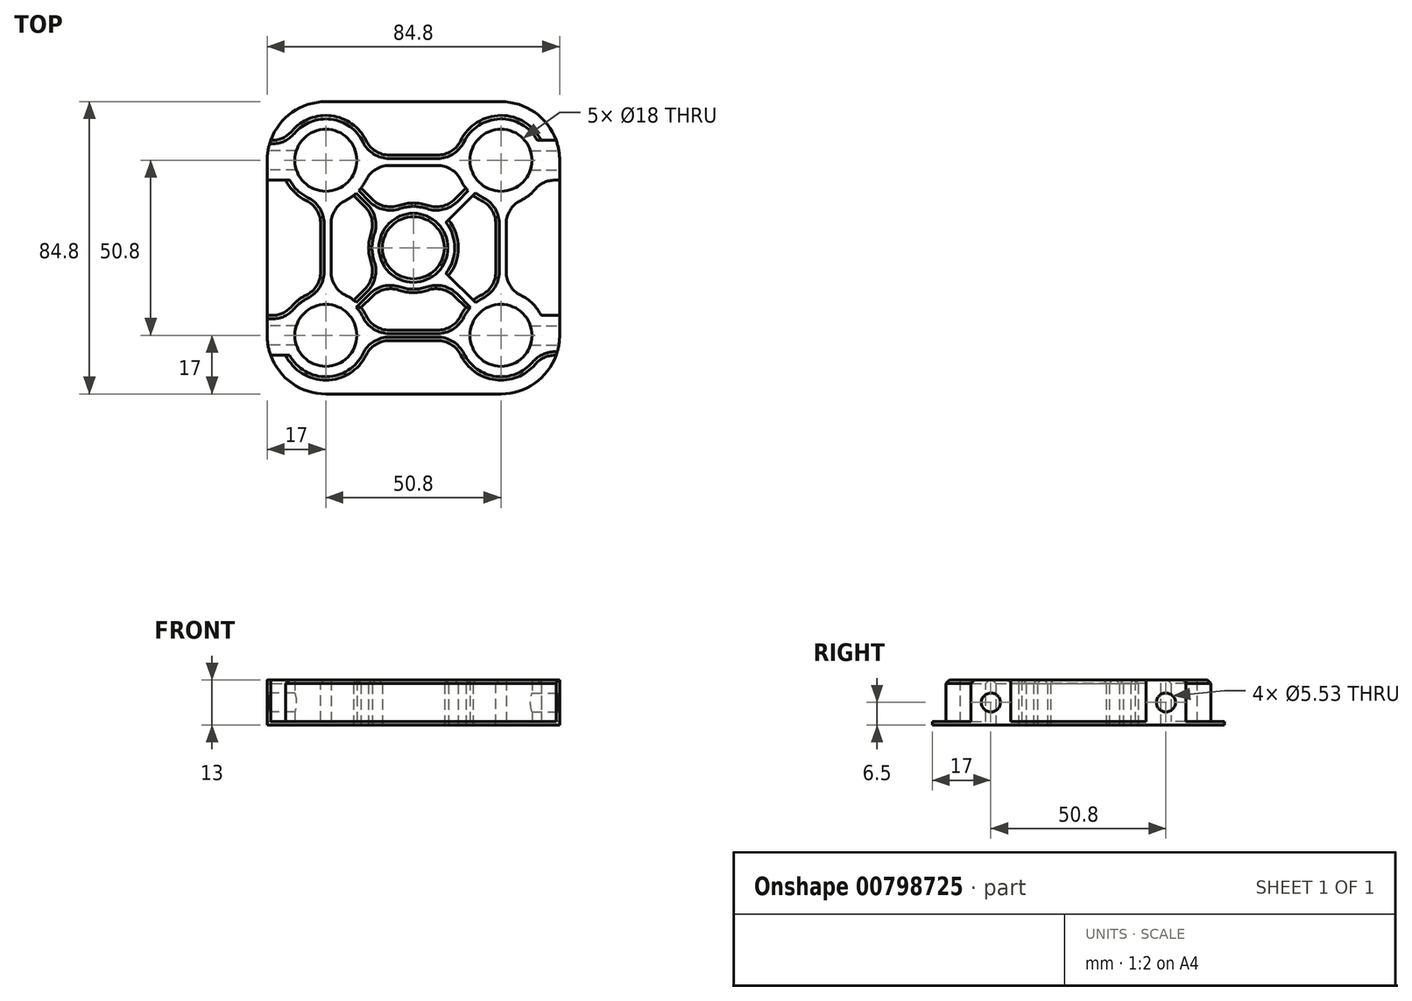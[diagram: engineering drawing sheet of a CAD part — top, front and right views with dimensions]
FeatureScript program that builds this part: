
annotation { "Feature Type Name" : "Feature", "Feature Type Description" : "" }
export const myFeature = defineFeature(function(context is Context, id is Id, definition is map)
    precondition{}
    {
        {
            var Q0;
            Q0=qCreatedBy(makeId("Top.planeOp"),FACE);
            var sketch = newSketch(context, id + "F0", { "sketchPlane" : qUnion([Q0])});
            skLineSegment(sketch, "E0.bottom", {"start": v(25.4, -25.4) * mm, "end": v(-25.4, -25.4) * mm, "construction": true});
            skLineSegment(sketch, "E0.top", {"start": v(25.4, 25.4) * mm, "end": v(-25.4, 25.4) * mm, "construction": true});
            skLineSegment(sketch, "E0.left", {"start": v(25.4, -25.4) * mm, "end": v(25.4, 25.4) * mm, "construction": true});
            skLineSegment(sketch, "E0.right", {"start": v(-25.4, -25.4) * mm, "end": v(-25.4, 25.4) * mm, "construction": true});
            skPoint(sketch, "E0.middle", {"position": v(0, 0) * mm});
            skPoint(sketch, "E1.middle", {"position": v(-41.65, 39) * mm});
            skCircle(sketch, "E2", {"center": v(-25.4, 25.4) * mm, "radius": 9 * mm});
            skCircle(sketch, "E3", {"center": v(25.4, 25.4) * mm, "radius": 9 * mm});
            skCircle(sketch, "E4", {"center": v(25.4, -25.4) * mm, "radius": 9 * mm});
            skCircle(sketch, "E5", {"center": v(-25.4, -25.4) * mm, "radius": 9 * mm});
            skCircle(sketch, "E6", {"center": v(0, 0) * mm, "radius": 9 * mm});
            skSolve(sketch);
        }
        {
            var Q0;
            Q0=qCreatedBy(makeId("Top.planeOp"),FACE);
            var sketch = newSketch(context, id + "F1", { "sketchPlane" : qUnion([Q0])});
            skLineSegment(sketch, "E7.bottom", {"start": v(25.4, -42.4) * mm, "end": v(-25.4, -42.4) * mm});
            skLineSegment(sketch, "E7.top", {"start": v(25.4, 42.4) * mm, "end": v(-25.4, 42.4) * mm});
            skLineSegment(sketch, "E7.left", {"start": v(42.4, -25.4) * mm, "end": v(42.4, 25.4) * mm});
            skLineSegment(sketch, "E7.right", {"start": v(-42.4, -25.4) * mm, "end": v(-42.4, 25.4) * mm});
            skPoint(sketch, "E7.middle", {"position": v(0, 0) * mm});
            skPoint(sketch, "E8.visualSharp", {"position": v(42.4, 42.4) * mm});
            skArc(sketch, "E8.filletArc", {"start": v(42.4, 25.4) * mm, "mid": v(37.42, 37.42) * mm, "end": v(25.4, 42.4) * mm});
            skPoint(sketch, "E9.visualSharp", {"position": v(42.4, -42.4) * mm});
            skArc(sketch, "E9.filletArc", {"start": v(25.4, -42.4) * mm, "mid": v(37.42, -37.42) * mm, "end": v(42.4, -25.4) * mm});
            skPoint(sketch, "E10.visualSharp", {"position": v(-42.4, -42.4) * mm});
            skArc(sketch, "E10.filletArc", {"start": v(-42.4, -25.4) * mm, "mid": v(-37.42, -37.42) * mm, "end": v(-25.4, -42.4) * mm});
            skPoint(sketch, "E11.visualSharp", {"position": v(-42.4, 42.4) * mm});
            skArc(sketch, "E11.filletArc", {"start": v(-25.4, 42.4) * mm, "mid": v(-37.42, 37.42) * mm, "end": v(-42.4, 25.4) * mm});
            skSolve(sketch);
        }
        {
            var Q0;
            Q0 = qSketchRegion(id + "F1", true);
            extrude(context, id + "F2", {"entities" : qUnion([Q0]), "depth" : 1 * mm, "offsetDistance" : 25 * mm});
        }
        {
            var Q0;
            Q0 = qSketchRegion(id + "F0", true);
            extrude(context, id + "F3", {"entities" : qUnion([Q0]), "operationType" : NewBodyOperationType.REMOVE, "depth" : 25 * mm, "offsetDistance" : 25 * mm});
        }
        {
            var Q0;
            Q0=makeQuery(id+"F2.opExtrude","CAP_FACE",FACE,{"disambiguationData":[OSD([sQuery(id+"F1.wireOp",EDGE,"E7.bottom"),sQuery(id+"F1.wireOp",EDGE,"E7.top"),sQuery(id+"F1.wireOp",EDGE,"E7.left"),sQuery(id+"F1.wireOp",EDGE,"E7.right"),sQuery(id+"F1.wireOp",EDGE,"E8.filletArc"),sQuery(id+"F1.wireOp",EDGE,"E9.filletArc"),sQuery(id+"F1.wireOp",EDGE,"E10.filletArc"),sQuery(id+"F1.wireOp",EDGE,"E11.filletArc")])],"isStart":false});
            var sketch = newSketch(context, id + "F4", { "sketchPlane" : qUnion([Q0])});
            skArc(sketch, "E12", {"start": v(-12.49, 26.9) * mm, "mid": v(-34.6, 34.6) * mm, "end": v(-26.9, 12.49) * mm});
            skArc(sketch, "E13", {"start": v(12.49, 23.9) * mm, "mid": v(16.2, 16.2) * mm, "end": v(23.9, 12.49) * mm});
            skArc(sketch, "E14", {"start": v(23.9, -12.49) * mm, "mid": v(16.2, -16.2) * mm, "end": v(12.49, -23.9) * mm});
            skArc(sketch, "E15", {"start": v(-12.49, -23.9) * mm, "mid": v(-16.2, -16.2) * mm, "end": v(-23.9, -12.49) * mm});
            skCircle(sketch, "E16", {"center": v(0, 0) * mm, "radius": 13 * mm});
            skCircle(sketch, "E17.0", {"center": v(-25.4, 25.4) * mm, "radius": 9 * mm});
            skCircle(sketch, "E18.0", {"center": v(25.4, 25.4) * mm, "radius": 9 * mm});
            skCircle(sketch, "E19.0", {"center": v(25.4, -25.4) * mm, "radius": 9 * mm});
            skCircle(sketch, "E20.0", {"center": v(-25.4, -25.4) * mm, "radius": 9 * mm});
            skLineSegment(sketch, "E21", {"start": v(-26.9, 12.49) * mm, "end": v(-26.9, -12.49) * mm});
            skLineSegment(sketch, "E22", {"start": v(-23.9, 12.49) * mm, "end": v(-23.9, -12.49) * mm});
            skLineSegment(sketch, "E23", {"start": v(-12.49, 26.9) * mm, "end": v(12.49, 26.9) * mm});
            skLineSegment(sketch, "E24", {"start": v(-12.49, 23.9) * mm, "end": v(12.49, 23.9) * mm});
            skLineSegment(sketch, "E25", {"start": v(23.9, 12.49) * mm, "end": v(23.9, -12.49) * mm});
            skLineSegment(sketch, "E26", {"start": v(26.9, 12.49) * mm, "end": v(26.9, -12.49) * mm});
            skLineSegment(sketch, "E27", {"start": v(-12.49, -23.9) * mm, "end": v(12.49, -23.9) * mm});
            skLineSegment(sketch, "E28", {"start": v(-12.49, -26.9) * mm, "end": v(12.49, -26.9) * mm});
            skCircle(sketch, "E29.0", {"center": v(0, 0) * mm, "radius": 9 * mm});
            skArc(sketch, "E30.trimOffspring", {"start": v(-23.9, 12.49) * mm, "mid": v(-16.2, 16.2) * mm, "end": v(-12.49, 23.9) * mm});
            skArc(sketch, "E31.trimOffspring", {"start": v(26.9, 12.49) * mm, "mid": v(34.6, 34.6) * mm, "end": v(12.49, 26.9) * mm});
            skArc(sketch, "E32.trimOffspring", {"start": v(12.49, -26.9) * mm, "mid": v(34.6, -34.6) * mm, "end": v(26.9, -12.49) * mm});
            skArc(sketch, "E33.trimOffspring", {"start": v(-26.9, -12.49) * mm, "mid": v(-34.6, -34.6) * mm, "end": v(-12.49, -26.9) * mm});
            skSolve(sketch);
        }
        {
            var Q0;
            Q0=makeQuery(id+"F4.imprint","IMPRINT",FACE,{"disambiguationData":[TD([[makeQuery(id+"F4.imprint","IMPRINT",EDGE,{"derivedFrom":sQuery(id+"F4.wireOp",EDGE,"E12")}),-1.0]])]});
            var sketch = newSketch(context, id + "F5", { "sketchPlane" : qUnion([Q0])});
            skLineSegment(sketch, "E34.0", {"start": v(-42.4, -25.4) * mm, "end": v(-42.4, -19.64) * mm});
            skArc(sketch, "E35.0", {"start": v(-42.4, -25.4) * mm, "mid": v(-42.15, -28.32) * mm, "end": v(-41.4, -31.16) * mm});
            skArc(sketch, "E36.0", {"start": v(-37.05, -19.64) * mm, "mid": v(-38.4, -25.4) * mm, "end": v(-37.05, -31.16) * mm});
            skLineSegment(sketch, "E37", {"start": v(-42.4, -19.64) * mm, "end": v(-37.05, -19.64) * mm});
            skLineSegment(sketch, "E38", {"start": v(-41.4, -31.16) * mm, "end": v(-37.05, -31.16) * mm});
            skPoint(sketch, "E39.orphan", {"position": v(-42.4, 25.4) * mm});
            skPoint(sketch, "E40.orphan", {"position": v(-26.9, -12.49) * mm});
            skPoint(sketch, "E41.orphan", {"position": v(-25.4, -42.4) * mm});
            skPoint(sketch, "E42.orphan", {"position": v(-12.49, -26.9) * mm});
            skLineSegment(sketch, "E43.MirrorCS", {"start": v(42.4, -25.4) * mm, "end": v(42.4, -19.64) * mm});
            skLineSegment(sketch, "E44.MirrorCS", {"start": v(42.4, -19.64) * mm, "end": v(37.05, -19.64) * mm});
            skLineSegment(sketch, "E45.MirrorCS", {"start": v(41.4, -31.16) * mm, "end": v(37.05, -31.16) * mm});
            skArc(sketch, "E46.MirrorCS", {"start": v(37.05, -19.64) * mm, "mid": v(38.4, -25.4) * mm, "end": v(37.05, -31.16) * mm});
            skArc(sketch, "E47.MirrorCS", {"start": v(42.4, -25.4) * mm, "mid": v(42.15, -28.32) * mm, "end": v(41.4, -31.16) * mm});
            skLineSegment(sketch, "E48.MirrorCS", {"start": v(-41.4, 31.16) * mm, "end": v(-37.05, 31.16) * mm});
            skPoint(sketch, "E49.MirrorP", {"position": v(-12.49, 26.9) * mm});
            skLineSegment(sketch, "E50.MirrorCS", {"start": v(42.4, 25.4) * mm, "end": v(42.4, 19.64) * mm});
            skLineSegment(sketch, "E51.MirrorCS", {"start": v(-42.4, 19.64) * mm, "end": v(-37.05, 19.64) * mm});
            skArc(sketch, "E52.MirrorCS", {"start": v(37.05, 19.64) * mm, "mid": v(38.4, 25.4) * mm, "end": v(37.05, 31.16) * mm});
            skArc(sketch, "E53.MirrorCS", {"start": v(-42.4, 25.4) * mm, "mid": v(-42.15, 28.32) * mm, "end": v(-41.4, 31.16) * mm});
            skLineSegment(sketch, "E54.MirrorCS", {"start": v(-42.4, 25.4) * mm, "end": v(-42.4, 19.64) * mm});
            skLineSegment(sketch, "E55.MirrorCS", {"start": v(42.4, 19.64) * mm, "end": v(37.05, 19.64) * mm});
            skLineSegment(sketch, "E56.MirrorCS", {"start": v(41.4, 31.16) * mm, "end": v(37.05, 31.16) * mm});
            skArc(sketch, "E57.MirrorCS", {"start": v(42.4, 25.4) * mm, "mid": v(42.15, 28.32) * mm, "end": v(41.4, 31.16) * mm});
            skArc(sketch, "E58.MirrorCS", {"start": v(-37.05, 19.64) * mm, "mid": v(-38.4, 25.4) * mm, "end": v(-37.05, 31.16) * mm});
            skSolve(sketch);
        }
        {
            var Q0;
            Q0 = qSketchRegion(id + "F4", true);
            var Q1;
            Q1=makeQuery(id+"F4.imprint","IMPRINT",FACE,{"disambiguationData":[TD([[makeQuery(id+"F4.imprint","IMPRINT",EDGE,{"derivedFrom":sQuery(id+"F4.wireOp",EDGE,"E16")}),1.0]])]});
            extrude(context, id + "F6", {"entities" : qUnion([Q0, Q1]), "operationType" : NewBodyOperationType.ADD, "depth" : 12 * mm, "offsetDistance" : 25 * mm});
        }
        {
            var Q0;
            Q0 = qSketchRegion(id + "F5", true);
            var Q1;
            Q1=makeQuery(id+"F6.opExtrude","CAP_FACE",FACE,{"disambiguationData":[OSD([sQuery(id+"F4.wireOp",EDGE,"E12"),sQuery(id+"F4.wireOp",EDGE,"E13"),sQuery(id+"F4.wireOp",EDGE,"E14"),sQuery(id+"F4.wireOp",EDGE,"E15"),sQuery(id+"F4.wireOp",EDGE,"E17.0"),sQuery(id+"F4.wireOp",EDGE,"E18.0"),sQuery(id+"F4.wireOp",EDGE,"E19.0"),sQuery(id+"F4.wireOp",EDGE,"E20.0"),sQuery(id+"F4.wireOp",EDGE,"E21"),sQuery(id+"F4.wireOp",EDGE,"E22"),sQuery(id+"F4.wireOp",EDGE,"E23"),sQuery(id+"F4.wireOp",EDGE,"E24"),sQuery(id+"F4.wireOp",EDGE,"E25"),sQuery(id+"F4.wireOp",EDGE,"E26"),sQuery(id+"F4.wireOp",EDGE,"E27"),sQuery(id+"F4.wireOp",EDGE,"E28"),sQuery(id+"F4.wireOp",EDGE,"E30.trimOffspring"),sQuery(id+"F4.wireOp",EDGE,"E31.trimOffspring"),sQuery(id+"F4.wireOp",EDGE,"E32.trimOffspring"),sQuery(id+"F4.wireOp",EDGE,"E33.trimOffspring")])],"isStart":false});
            extrude(context, id + "F7", {"entities" : qUnion([Q0]), "operationType" : NewBodyOperationType.ADD, "endBound" : BoundingType.UP_TO_SURFACE, "depth" : 25 * mm, "endBoundEntityFace" : qUnion([Q1]), "offsetDistance" : 25 * mm});
        }
        {
            var Q0;
            Q0=makeQuery(id+"F7.boolean.opBoolean","MERGE",FACE,{"derivedFrom":[makeQuery(id+"F2.opExtrude","SWEPT_FACE",FACE,{"disambiguationData":[OSD([sQuery(id+"F1.wireOp",EDGE,"E7.right")])]}),makeQuery(id+"F7.opExtrude","SWEPT_FACE",FACE,{"disambiguationData":[OSD([sQuery(id+"F5.wireOp",EDGE,"E34.0")])]}),makeQuery(id+"F7.opExtrude","SWEPT_FACE",FACE,{"disambiguationData":[OSD([sQuery(id+"F5.wireOp",EDGE,"E54.MirrorCS")])]})]});
            cPlane(context, id + "F8", {"entities" : qUnion([Q0]), "cplaneType" : CPlaneType.OFFSET, "offset" : 0 * mm, "width" : 150 * mm, "height" : 150 * mm});
        }
        {
            var Q0;
            Q0=qCreatedBy(id+"F8.planeOp",FACE);
            var sketch = newSketch(context, id + "F9", { "sketchPlane" : qUnion([Q0])});
            skCircle(sketch, "E59", {"center": v(-25.4, 6.5) * mm, "radius": 2.76 * mm});
            skCircle(sketch, "E60", {"center": v(25.4, 6.5) * mm, "radius": 2.76 * mm});
            skLineSegment(sketch, "E61.0", {"start": v(-25.4, 13) * mm, "end": v(-25.4, 0) * mm, "construction": true});
            skLineSegment(sketch, "E62.0", {"start": v(25.4, 13) * mm, "end": v(25.4, 0) * mm, "construction": true});
            skLineSegment(sketch, "E63", {"start": v(-25.4, 6.5) * mm, "end": v(25.4, 6.5) * mm, "construction": true});
            skSolve(sketch);
        }
        {
            var Q0;
            Q0=makeQuery(id+"F7.boolean.opBoolean","MERGE",FACE,{"derivedFrom":[makeQuery(id+"F2.opExtrude","SWEPT_FACE",FACE,{"disambiguationData":[OSD([sQuery(id+"F1.wireOp",EDGE,"E7.left")])]}),makeQuery(id+"F7.opExtrude","SWEPT_FACE",FACE,{"disambiguationData":[OSD([sQuery(id+"F5.wireOp",EDGE,"E43.MirrorCS")])]}),makeQuery(id+"F7.opExtrude","SWEPT_FACE",FACE,{"disambiguationData":[OSD([sQuery(id+"F5.wireOp",EDGE,"E50.MirrorCS")])]})]});
            cPlane(context, id + "F10", {"entities" : qUnion([Q0]), "cplaneType" : CPlaneType.OFFSET, "offset" : 0 * mm, "width" : 150 * mm, "height" : 150 * mm});
        }
        {
            var Q0;
            Q0=qCreatedBy(id+"F10.planeOp",FACE);
            var sketch = newSketch(context, id + "F11", { "sketchPlane" : qUnion([Q0])});
            skCircle(sketch, "E64.0", {"center": v(-25.4, 6.5) * mm, "radius": 2.76 * mm});
            skCircle(sketch, "E65.0", {"center": v(25.4, 6.5) * mm, "radius": 2.76 * mm});
            skSolve(sketch);
        }
        {
            var Q0;
            Q0 = qSketchRegion(id + "F9", true);
            extrude(context, id + "F12", {"entities" : qUnion([Q0]), "operationType" : NewBodyOperationType.REMOVE, "oppositeDirection" : true, "depth" : 20 * mm, "offsetDistance" : 25 * mm});
        }
        {
            var Q0;
            Q0 = qSketchRegion(id + "F11", true);
            extrude(context, id + "F13", {"entities" : qUnion([Q0]), "operationType" : NewBodyOperationType.REMOVE, "oppositeDirection" : true, "depth" : 15 * mm, "offsetDistance" : 25 * mm});
        }
        {
            var Q0;
            Q0=makeQuery(id+"F2.opExtrude","CAP_FACE",FACE,{"disambiguationData":[OSD([sQuery(id+"F1.wireOp",EDGE,"E7.bottom"),sQuery(id+"F1.wireOp",EDGE,"E7.top"),sQuery(id+"F1.wireOp",EDGE,"E7.left"),sQuery(id+"F1.wireOp",EDGE,"E7.right"),sQuery(id+"F1.wireOp",EDGE,"E8.filletArc"),sQuery(id+"F1.wireOp",EDGE,"E9.filletArc"),sQuery(id+"F1.wireOp",EDGE,"E10.filletArc"),sQuery(id+"F1.wireOp",EDGE,"E11.filletArc")])],"isStart":true});
            var sketch = newSketch(context, id + "F14", { "sketchPlane" : qUnion([Q0])});
            skCircle(sketch, "E66", {"center": v(0, 0) * mm, "radius": 18.5 * mm, "construction": true});
            skCircle(sketch, "E67", {"center": v(18.5, 0) * mm, "radius": 5 * mm});
            skCircle(sketch, "E68", {"center": v(0, 18.5) * mm, "radius": 5 * mm});
            skCircle(sketch, "E69", {"center": v(-18.5, 0) * mm, "radius": 5 * mm});
            skCircle(sketch, "E70", {"center": v(0, -18.5) * mm, "radius": 5 * mm});
            skSolve(sketch);
        }
        {
            var Q0;
            Q0=makeQuery(id+"F6.boolean.opBoolean","SPLIT",FACE,{"disambiguationData":[TD([makeQuery(id+"F6.opExtrude","SWEPT_FACE",FACE,{"disambiguationData":[OSD([sQuery(id+"F4.wireOp",EDGE,"E13")])]})])],"derivedFrom":makeQuery(id+"F2.opExtrude","CAP_FACE",FACE,{"disambiguationData":[OSD([sQuery(id+"F1.wireOp",EDGE,"E7.bottom"),sQuery(id+"F1.wireOp",EDGE,"E7.top"),sQuery(id+"F1.wireOp",EDGE,"E7.left"),sQuery(id+"F1.wireOp",EDGE,"E7.right"),sQuery(id+"F1.wireOp",EDGE,"E8.filletArc"),sQuery(id+"F1.wireOp",EDGE,"E9.filletArc"),sQuery(id+"F1.wireOp",EDGE,"E10.filletArc"),sQuery(id+"F1.wireOp",EDGE,"E11.filletArc")])],"isStart":false})});
            var sketch = newSketch(context, id + "F15", { "sketchPlane" : qUnion([Q0])});
            skLineSegment(sketch, "E71", {"start": v(-25.4, 25.4) * mm, "end": v(25.4, -25.4) * mm, "construction": true});
            skLineSegment(sketch, "E72", {"start": v(25.4, 25.4) * mm, "end": v(-25.4, -25.4) * mm, "construction": true});
            skLineSegment(sketch, "E73", {"start": v(8.07, 10.2) * mm, "end": v(15.2, 17.33) * mm});
            skLineSegment(sketch, "E74", {"start": v(17.33, 15.2) * mm, "end": v(10.2, 8.07) * mm});
            skLineSegment(sketch, "E75", {"start": v(-17.33, -15.2) * mm, "end": v(-10.2, -8.07) * mm});
            skLineSegment(sketch, "E76", {"start": v(-15.2, -17.33) * mm, "end": v(-8.07, -10.2) * mm});
            skArc(sketch, "E77.0", {"start": v(15.2, 17.33) * mm, "mid": v(16.2, 16.2) * mm, "end": v(17.33, 15.2) * mm});
            skArc(sketch, "E78.0", {"start": v(8.07, -10.2) * mm, "mid": v(9.2, -9.2) * mm, "end": v(10.2, -8.07) * mm});
            skArc(sketch, "E79.0", {"start": v(-15.2, -17.33) * mm, "mid": v(-16.2, -16.2) * mm, "end": v(-17.33, -15.2) * mm});
            skPoint(sketch, "E80.orphan", {"position": v(-23.9, -12.49) * mm});
            skPoint(sketch, "E81.orphan", {"position": v(-12.49, -23.9) * mm});
            skLineSegment(sketch, "E82", {"start": v(8.07, -10.2) * mm, "end": v(15.2, -17.33) * mm});
            skLineSegment(sketch, "E83", {"start": v(10.2, -8.07) * mm, "end": v(17.33, -15.2) * mm});
            skLineSegment(sketch, "E84", {"start": v(-17.33, 15.2) * mm, "end": v(-10.2, 8.07) * mm});
            skLineSegment(sketch, "E85", {"start": v(-15.2, 17.33) * mm, "end": v(-8.07, 10.2) * mm});
            skArc(sketch, "E86.0", {"start": v(-17.33, 15.2) * mm, "mid": v(-16.2, 16.2) * mm, "end": v(-15.2, 17.33) * mm});
            skArc(sketch, "E87.0", {"start": v(17.33, -15.2) * mm, "mid": v(16.2, -16.2) * mm, "end": v(15.2, -17.33) * mm});
            skArc(sketch, "E88.trimOffspring", {"start": v(10.2, 8.07) * mm, "mid": v(9.2, 9.2) * mm, "end": v(8.07, 10.2) * mm});
            skArc(sketch, "E89.trimOffspring", {"start": v(-8.07, 10.2) * mm, "mid": v(-13, 0) * mm, "end": v(-8.07, -10.2) * mm});
            skPoint(sketch, "E90.orphan", {"position": v(12.49, 23.9) * mm});
            skPoint(sketch, "E91.orphan", {"position": v(23.9, 12.49) * mm});
            skPoint(sketch, "E92.orphan", {"position": v(-12.49, 23.9) * mm});
            skPoint(sketch, "E93.orphan", {"position": v(-23.9, 12.49) * mm});
            skPoint(sketch, "E94.orphan", {"position": v(12.49, -23.9) * mm});
            skPoint(sketch, "E95.orphan", {"position": v(23.9, -12.49) * mm});
            skSolve(sketch);
        }
        {
            var Q0;
            Q0 = qSketchRegion(id + "F15", true);
            var Q1;
            {var subQ0=sQuery(id+"F4.wireOp",EDGE,"E33.trimOffspring");var subQ1=sQuery(id+"F4.wireOp",EDGE,"E32.trimOffspring");var subQ2=sQuery(id+"F4.wireOp",EDGE,"E31.trimOffspring");var subQ3=sQuery(id+"F4.wireOp",EDGE,"E30.trimOffspring");var subQ4=sQuery(id+"F4.wireOp",EDGE,"E28");var subQ5=sQuery(id+"F4.wireOp",EDGE,"E27");var subQ6=sQuery(id+"F4.wireOp",EDGE,"E26");var subQ7=sQuery(id+"F4.wireOp",EDGE,"E25");var subQ8=sQuery(id+"F4.wireOp",EDGE,"E24");var subQ9=sQuery(id+"F4.wireOp",EDGE,"E23");var subQ10=sQuery(id+"F4.wireOp",EDGE,"E22");var subQ11=sQuery(id+"F4.wireOp",EDGE,"E21");var subQ12=sQuery(id+"F4.wireOp",EDGE,"E20.0");var subQ13=sQuery(id+"F4.wireOp",EDGE,"E19.0");var subQ14=sQuery(id+"F4.wireOp",EDGE,"E18.0");var subQ15=sQuery(id+"F4.wireOp",EDGE,"E17.0");var subQ16=sQuery(id+"F4.wireOp",EDGE,"E15");var subQ17=sQuery(id+"F4.wireOp",EDGE,"E14");var subQ18=sQuery(id+"F4.wireOp",EDGE,"E13");var subQ19=sQuery(id+"F4.wireOp",EDGE,"E12");Q1=makeQuery(id+"F7.boolean.opBoolean","MERGE",FACE,{"derivedFrom":[makeQuery(id+"F6.opExtrude","CAP_FACE",FACE,{"disambiguationData":[OSD([subQ19,subQ18,subQ17,subQ16,subQ15,subQ14,subQ13,subQ12,subQ11,subQ10,subQ9,subQ8,subQ7,subQ6,subQ5,subQ4,subQ3,subQ2,subQ1,subQ0])],"isStart":false}),makeQuery(id+"F7.opExtrude","CAP_FACE",FACE,{"disambiguationData":[OSD([subQ19,subQ18,subQ17,subQ16,subQ15,subQ14,subQ13,subQ12,subQ11,subQ10,subQ9,subQ8,subQ7,subQ6,subQ5,subQ4,subQ3,subQ2,subQ1,subQ0]),OD(0.0)],"isStart":false}),makeQuery(id+"F7.opExtrude","CAP_FACE",FACE,{"disambiguationData":[OSD([subQ19,subQ18,subQ17,subQ16,subQ15,subQ14,subQ13,subQ12,subQ11,subQ10,subQ9,subQ8,subQ7,subQ6,subQ5,subQ4,subQ3,subQ2,subQ1,subQ0]),OD(1.0)],"isStart":false}),makeQuery(id+"F7.opExtrude","CAP_FACE",FACE,{"disambiguationData":[OSD([subQ19,subQ18,subQ17,subQ16,subQ15,subQ14,subQ13,subQ12,subQ11,subQ10,subQ9,subQ8,subQ7,subQ6,subQ5,subQ4,subQ3,subQ2,subQ1,subQ0]),OD(2.0)],"isStart":false}),makeQuery(id+"F7.opExtrude","CAP_FACE",FACE,{"disambiguationData":[OSD([subQ19,subQ18,subQ17,subQ16,subQ15,subQ14,subQ13,subQ12,subQ11,subQ10,subQ9,subQ8,subQ7,subQ6,subQ5,subQ4,subQ3,subQ2,subQ1,subQ0]),OD(3.0)],"isStart":false})]});}
            extrude(context, id + "F16", {"entities" : qUnion([Q0]), "operationType" : NewBodyOperationType.ADD, "endBound" : BoundingType.UP_TO_SURFACE, "depth" : 25 * mm, "endBoundEntityFace" : qUnion([Q1]), "offsetDistance" : 25 * mm});
        }
        {
            var Q0;
            {var subQ2=makeQuery(id+"F6.opExtrude","SWEPT_FACE",FACE,{"disambiguationData":[OSD([sQuery(id+"F4.wireOp",EDGE,"E27")])]});Q0=makeQuery(id+"F16.boolean.opBoolean","SPLIT",FACE,{"disambiguationData":[TD([subQ2])],"derivedFrom":makeQuery(id+"F6.boolean.opBoolean","SPLIT",FACE,{"disambiguationData":[TD([makeQuery(id+"F6.opExtrude","SWEPT_FACE",FACE,{"disambiguationData":[OSD([sQuery(id+"F4.wireOp",EDGE,"E13")])]})])],"derivedFrom":makeQuery(id+"F2.opExtrude","CAP_FACE",FACE,{"disambiguationData":[OSD([sQuery(id+"F1.wireOp",EDGE,"E7.bottom"),sQuery(id+"F1.wireOp",EDGE,"E7.top"),sQuery(id+"F1.wireOp",EDGE,"E7.left"),sQuery(id+"F1.wireOp",EDGE,"E7.right"),sQuery(id+"F1.wireOp",EDGE,"E8.filletArc"),sQuery(id+"F1.wireOp",EDGE,"E9.filletArc"),sQuery(id+"F1.wireOp",EDGE,"E10.filletArc"),sQuery(id+"F1.wireOp",EDGE,"E11.filletArc")])],"isStart":false})})});}
            var Q1;
            {var subQ1=makeQuery(id+"F6.opExtrude","SWEPT_FACE",FACE,{"disambiguationData":[OSD([sQuery(id+"F4.wireOp",EDGE,"E22")])]});Q1=makeQuery(id+"F16.boolean.opBoolean","SPLIT",FACE,{"disambiguationData":[TD([subQ1])],"derivedFrom":makeQuery(id+"F6.boolean.opBoolean","SPLIT",FACE,{"disambiguationData":[TD([makeQuery(id+"F6.opExtrude","SWEPT_FACE",FACE,{"disambiguationData":[OSD([sQuery(id+"F4.wireOp",EDGE,"E13")])]})])],"derivedFrom":makeQuery(id+"F2.opExtrude","CAP_FACE",FACE,{"disambiguationData":[OSD([sQuery(id+"F1.wireOp",EDGE,"E7.bottom"),sQuery(id+"F1.wireOp",EDGE,"E7.top"),sQuery(id+"F1.wireOp",EDGE,"E7.left"),sQuery(id+"F1.wireOp",EDGE,"E7.right"),sQuery(id+"F1.wireOp",EDGE,"E8.filletArc"),sQuery(id+"F1.wireOp",EDGE,"E9.filletArc"),sQuery(id+"F1.wireOp",EDGE,"E10.filletArc"),sQuery(id+"F1.wireOp",EDGE,"E11.filletArc")])],"isStart":false})})});}
            var Q2;
            {var subQ1=makeQuery(id+"F6.opExtrude","SWEPT_FACE",FACE,{"disambiguationData":[OSD([sQuery(id+"F4.wireOp",EDGE,"E24")])]});var subQ3=makeQuery(id+"F6.opExtrude","SWEPT_FACE",FACE,{"disambiguationData":[OSD([sQuery(id+"F4.wireOp",EDGE,"E13")])]});Q2=makeQuery(id+"F16.boolean.opBoolean","SPLIT",FACE,{"disambiguationData":[TD([subQ1])],"derivedFrom":makeQuery(id+"F6.boolean.opBoolean","SPLIT",FACE,{"disambiguationData":[TD([subQ3])],"derivedFrom":makeQuery(id+"F2.opExtrude","CAP_FACE",FACE,{"disambiguationData":[OSD([sQuery(id+"F1.wireOp",EDGE,"E7.bottom"),sQuery(id+"F1.wireOp",EDGE,"E7.top"),sQuery(id+"F1.wireOp",EDGE,"E7.left"),sQuery(id+"F1.wireOp",EDGE,"E7.right"),sQuery(id+"F1.wireOp",EDGE,"E8.filletArc"),sQuery(id+"F1.wireOp",EDGE,"E9.filletArc"),sQuery(id+"F1.wireOp",EDGE,"E10.filletArc"),sQuery(id+"F1.wireOp",EDGE,"E11.filletArc")])],"isStart":false})})});}
            var Q3;
            {var subQ0=makeQuery(id+"F6.opExtrude","SWEPT_FACE",FACE,{"disambiguationData":[OSD([sQuery(id+"F4.wireOp",EDGE,"E25")])]});var subQ3=makeQuery(id+"F6.opExtrude","SWEPT_FACE",FACE,{"disambiguationData":[OSD([sQuery(id+"F4.wireOp",EDGE,"E13")])]});Q3=makeQuery(id+"F16.boolean.opBoolean","SPLIT",FACE,{"disambiguationData":[TD([subQ0])],"derivedFrom":makeQuery(id+"F6.boolean.opBoolean","SPLIT",FACE,{"disambiguationData":[TD([subQ3])],"derivedFrom":makeQuery(id+"F2.opExtrude","CAP_FACE",FACE,{"disambiguationData":[OSD([sQuery(id+"F1.wireOp",EDGE,"E7.bottom"),sQuery(id+"F1.wireOp",EDGE,"E7.top"),sQuery(id+"F1.wireOp",EDGE,"E7.left"),sQuery(id+"F1.wireOp",EDGE,"E7.right"),sQuery(id+"F1.wireOp",EDGE,"E8.filletArc"),sQuery(id+"F1.wireOp",EDGE,"E9.filletArc"),sQuery(id+"F1.wireOp",EDGE,"E10.filletArc"),sQuery(id+"F1.wireOp",EDGE,"E11.filletArc")])],"isStart":false})})});}
            extrude(context, id + "F17", {"entities" : qUnion([Q0, Q1, Q2, Q3]), "operationType" : NewBodyOperationType.REMOVE, "oppositeDirection" : true, "depth" : 25 * mm, "offsetDistance" : 25 * mm});
        }
        {
            var Q0;
            Q0 = qSketchRegion(id + "F14", true);
            extrude(context, id + "F18", {"entities" : qUnion([Q0]), "operationType" : NewBodyOperationType.REMOVE, "oppositeDirection" : true, "depth" : 25 * mm, "offsetDistance" : 25 * mm});
        }
        {
            var Q0;
            Q0=makeQuery(id+"F6.opExtrude","SWEPT_EDGE",EDGE,{"disambiguationData":[OSD([sQuery(id+"F4.wireOp",EDGE,"E26"),sQuery(id+"F4.wireOp",EDGE,"E31.trimOffspring")])]});
            var Q1;
            Q1=makeQuery(id+"F6.opExtrude","SWEPT_EDGE",EDGE,{"disambiguationData":[OSD([sQuery(id+"F4.wireOp",EDGE,"E26"),sQuery(id+"F4.wireOp",EDGE,"E32.trimOffspring")])]});
            var Q2;
            Q2=makeQuery(id+"F6.opExtrude","SWEPT_EDGE",EDGE,{"disambiguationData":[OSD([sQuery(id+"F4.wireOp",EDGE,"E15"),sQuery(id+"F4.wireOp",EDGE,"E27")])]});
            var Q3;
            Q3=makeQuery(id+"F6.opExtrude","SWEPT_EDGE",EDGE,{"disambiguationData":[OSD([sQuery(id+"F4.wireOp",EDGE,"E15"),sQuery(id+"F4.wireOp",EDGE,"E22")])]});
            var Q4;
            Q4=makeQuery(id+"F6.opExtrude","SWEPT_EDGE",EDGE,{"disambiguationData":[OSD([sQuery(id+"F4.wireOp",EDGE,"E22"),sQuery(id+"F4.wireOp",EDGE,"E30.trimOffspring")])]});
            var Q5;
            Q5=makeQuery(id+"F6.opExtrude","SWEPT_EDGE",EDGE,{"disambiguationData":[OSD([sQuery(id+"F4.wireOp",EDGE,"E24"),sQuery(id+"F4.wireOp",EDGE,"E30.trimOffspring")])]});
            var Q6;
            Q6=makeQuery(id+"F6.opExtrude","SWEPT_EDGE",EDGE,{"disambiguationData":[OSD([sQuery(id+"F4.wireOp",EDGE,"E14"),sQuery(id+"F4.wireOp",EDGE,"E27")])]});
            var Q7;
            Q7=makeQuery(id+"F6.opExtrude","SWEPT_EDGE",EDGE,{"disambiguationData":[OSD([sQuery(id+"F4.wireOp",EDGE,"E14"),sQuery(id+"F4.wireOp",EDGE,"E25")])]});
            var Q8;
            Q8=makeQuery(id+"F6.opExtrude","SWEPT_EDGE",EDGE,{"disambiguationData":[OSD([sQuery(id+"F4.wireOp",EDGE,"E28"),sQuery(id+"F4.wireOp",EDGE,"E33.trimOffspring")])]});
            var Q9;
            Q9=makeQuery(id+"F6.opExtrude","SWEPT_EDGE",EDGE,{"disambiguationData":[OSD([sQuery(id+"F4.wireOp",EDGE,"E28"),sQuery(id+"F4.wireOp",EDGE,"E32.trimOffspring")])]});
            var Q10;
            Q10=makeQuery(id+"F7.opExtrude","SWEPT_EDGE",EDGE,{"disambiguationData":[OSD([sQuery(id+"F4.wireOp",EDGE,"E33.trimOffspring"),sQuery(id+"F5.wireOp",EDGE,"E36.0"),sQuery(id+"F5.wireOp",EDGE,"E38")])]});
            var Q11;
            Q11=makeQuery(id+"F7.opExtrude","SWEPT_EDGE",EDGE,{"disambiguationData":[OSD([sQuery(id+"F4.wireOp",EDGE,"E32.trimOffspring"),sQuery(id+"F5.wireOp",EDGE,"E45.MirrorCS"),sQuery(id+"F5.wireOp",EDGE,"E46.MirrorCS")])]});
            var Q12;
            Q12=makeQuery(id+"F7.opExtrude","SWEPT_EDGE",EDGE,{"disambiguationData":[OSD([sQuery(id+"F4.wireOp",EDGE,"E32.trimOffspring"),sQuery(id+"F5.wireOp",EDGE,"E44.MirrorCS"),sQuery(id+"F5.wireOp",EDGE,"E46.MirrorCS")])]});
            var Q13;
            Q13=makeQuery(id+"F7.opExtrude","SWEPT_EDGE",EDGE,{"disambiguationData":[OSD([sQuery(id+"F4.wireOp",EDGE,"E31.trimOffspring"),sQuery(id+"F5.wireOp",EDGE,"E52.MirrorCS"),sQuery(id+"F5.wireOp",EDGE,"E55.MirrorCS")])]});
            var Q14;
            Q14=makeQuery(id+"F6.opExtrude","SWEPT_EDGE",EDGE,{"disambiguationData":[OSD([sQuery(id+"F4.wireOp",EDGE,"E13"),sQuery(id+"F4.wireOp",EDGE,"E24")])]});
            var Q15;
            Q15=makeQuery(id+"F6.opExtrude","SWEPT_EDGE",EDGE,{"disambiguationData":[OSD([sQuery(id+"F4.wireOp",EDGE,"E23"),sQuery(id+"F4.wireOp",EDGE,"E31.trimOffspring")])]});
            var Q16;
            Q16=makeQuery(id+"F7.opExtrude","SWEPT_EDGE",EDGE,{"disambiguationData":[OSD([sQuery(id+"F4.wireOp",EDGE,"E12"),sQuery(id+"F5.wireOp",EDGE,"E48.MirrorCS"),sQuery(id+"F5.wireOp",EDGE,"E58.MirrorCS")])]});
            var Q17;
            Q17=makeQuery(id+"F6.opExtrude","SWEPT_EDGE",EDGE,{"disambiguationData":[OSD([sQuery(id+"F4.wireOp",EDGE,"E12"),sQuery(id+"F4.wireOp",EDGE,"E23")])]});
            var Q18;
            Q18=makeQuery(id+"F7.opExtrude","SWEPT_EDGE",EDGE,{"disambiguationData":[OSD([sQuery(id+"F4.wireOp",EDGE,"E31.trimOffspring"),sQuery(id+"F5.wireOp",EDGE,"E52.MirrorCS"),sQuery(id+"F5.wireOp",EDGE,"E56.MirrorCS")])]});
            var Q19;
            Q19=makeQuery(id+"F6.opExtrude","SWEPT_EDGE",EDGE,{"disambiguationData":[OSD([sQuery(id+"F4.wireOp",EDGE,"E12"),sQuery(id+"F4.wireOp",EDGE,"E21")])]});
            var Q20;
            Q20=makeQuery(id+"F6.opExtrude","SWEPT_EDGE",EDGE,{"disambiguationData":[OSD([sQuery(id+"F4.wireOp",EDGE,"E21"),sQuery(id+"F4.wireOp",EDGE,"E33.trimOffspring")])]});
            var Q21;
            Q21=makeQuery(id+"F7.opExtrude","SWEPT_EDGE",EDGE,{"disambiguationData":[OSD([sQuery(id+"F4.wireOp",EDGE,"E33.trimOffspring"),sQuery(id+"F5.wireOp",EDGE,"E36.0"),sQuery(id+"F5.wireOp",EDGE,"E37")])]});
            var Q22;
            {var subQ0=sQuery(id+"F15.wireOp",EDGE,"E89.trimOffspring");var subQ1=sQuery(id+"F15.wireOp",EDGE,"E84");Q22=makeQuery(id+"F17.boolean.opBoolean","MERGE",EDGE,{"derivedFrom":[makeQuery(id+"F16.opExtrude","SWEPT_EDGE",EDGE,{"disambiguationData":[OSD([subQ1,subQ0])]}),makeQuery(id+"F17.opExtrude","SWEPT_EDGE",EDGE,{"disambiguationData":[OSD([subQ1,subQ0])]})]});}
            var Q23;
            {var subQ0=sQuery(id+"F15.wireOp",EDGE,"E89.trimOffspring");var subQ1=sQuery(id+"F15.wireOp",EDGE,"E75");Q23=makeQuery(id+"F17.boolean.opBoolean","MERGE",EDGE,{"derivedFrom":[makeQuery(id+"F16.opExtrude","SWEPT_EDGE",EDGE,{"disambiguationData":[OSD([subQ1,subQ0])]}),makeQuery(id+"F17.opExtrude","SWEPT_EDGE",EDGE,{"disambiguationData":[OSD([subQ1,subQ0])]})]});}
            var Q24;
            {var subQ0=sQuery(id+"F15.wireOp",EDGE,"E89.trimOffspring");var subQ1=sQuery(id+"F15.wireOp",EDGE,"E76");var subQ2=sQuery(id+"F4.wireOp",EDGE,"E16");Q24=makeQuery(id+"F17.boolean.opBoolean","MERGE",EDGE,{"derivedFrom":[makeQuery(id+"F16.opExtrude","SWEPT_EDGE",EDGE,{"disambiguationData":[OSD([subQ2,subQ1,subQ0])]}),makeQuery(id+"F17.opExtrude","SWEPT_EDGE",EDGE,{"disambiguationData":[OSD([subQ2,subQ1,subQ0])]})]});}
            var Q25;
            {var subQ0=sQuery(id+"F15.wireOp",EDGE,"E82");var subQ1=sQuery(id+"F15.wireOp",EDGE,"E78.0");var subQ2=sQuery(id+"F4.wireOp",EDGE,"E16");Q25=makeQuery(id+"F17.boolean.opBoolean","MERGE",EDGE,{"derivedFrom":[makeQuery(id+"F16.opExtrude","SWEPT_EDGE",EDGE,{"disambiguationData":[OSD([subQ2,subQ1,subQ0])]}),makeQuery(id+"F17.opExtrude","SWEPT_EDGE",EDGE,{"disambiguationData":[OSD([subQ2,subQ1,subQ0])]})]});}
            var Q26;
            {var subQ0=sQuery(id+"F15.wireOp",EDGE,"E83");var subQ1=sQuery(id+"F15.wireOp",EDGE,"E78.0");var subQ2=sQuery(id+"F4.wireOp",EDGE,"E16");Q26=makeQuery(id+"F17.boolean.opBoolean","MERGE",EDGE,{"derivedFrom":[makeQuery(id+"F16.opExtrude","SWEPT_EDGE",EDGE,{"disambiguationData":[OSD([subQ2,subQ1,subQ0])]}),makeQuery(id+"F17.opExtrude","SWEPT_EDGE",EDGE,{"disambiguationData":[OSD([subQ2,subQ1,subQ0])]})]});}
            var Q27;
            {var subQ0=sQuery(id+"F15.wireOp",EDGE,"E88.trimOffspring");var subQ1=sQuery(id+"F15.wireOp",EDGE,"E74");var subQ2=sQuery(id+"F4.wireOp",EDGE,"E16");Q27=makeQuery(id+"F17.boolean.opBoolean","MERGE",EDGE,{"derivedFrom":[makeQuery(id+"F16.opExtrude","SWEPT_EDGE",EDGE,{"disambiguationData":[OSD([subQ2,subQ1,subQ0])]}),makeQuery(id+"F17.opExtrude","SWEPT_EDGE",EDGE,{"disambiguationData":[OSD([subQ2,subQ1,subQ0])]})]});}
            var Q28;
            {var subQ0=sQuery(id+"F15.wireOp",EDGE,"E88.trimOffspring");var subQ1=sQuery(id+"F15.wireOp",EDGE,"E73");var subQ2=sQuery(id+"F4.wireOp",EDGE,"E16");Q28=makeQuery(id+"F17.boolean.opBoolean","MERGE",EDGE,{"derivedFrom":[makeQuery(id+"F16.opExtrude","SWEPT_EDGE",EDGE,{"disambiguationData":[OSD([subQ2,subQ1,subQ0])]}),makeQuery(id+"F17.opExtrude","SWEPT_EDGE",EDGE,{"disambiguationData":[OSD([subQ2,subQ1,subQ0])]})]});}
            var Q29;
            {var subQ0=sQuery(id+"F15.wireOp",EDGE,"E89.trimOffspring");var subQ1=sQuery(id+"F15.wireOp",EDGE,"E85");var subQ2=sQuery(id+"F4.wireOp",EDGE,"E16");Q29=makeQuery(id+"F17.boolean.opBoolean","MERGE",EDGE,{"derivedFrom":[makeQuery(id+"F16.opExtrude","SWEPT_EDGE",EDGE,{"disambiguationData":[OSD([subQ2,subQ1,subQ0])]}),makeQuery(id+"F17.opExtrude","SWEPT_EDGE",EDGE,{"disambiguationData":[OSD([subQ2,subQ1,subQ0])]})]});}
            var Q30;
            {var subQ0=sQuery(id+"F4.wireOp",EDGE,"E25");var subQ1=sQuery(id+"F4.wireOp",EDGE,"E13");Q30=makeQuery(id+"F17.boolean.opBoolean","MERGE",EDGE,{"derivedFrom":[makeQuery(id+"F6.opExtrude","SWEPT_EDGE",EDGE,{"disambiguationData":[OSD([subQ1,subQ0])]}),makeQuery(id+"F17.opExtrude","SWEPT_EDGE",EDGE,{"disambiguationData":[OSD([subQ1,subQ0])]})]});}
            fillet(context, id + "F19", {"entities" : qUnion([Q0, Q1, Q2, Q3, Q4, Q5, Q6, Q7, Q8, Q9, Q10, Q11, Q12, Q13, Q14, Q15, Q16, Q17, Q18, Q19, Q20, Q21, Q22, Q23, Q24, Q25, Q26, Q27, Q28, Q29, Q30]), "radius" : 7.5 * mm, "tangentPropagation" : true, "allowEdgeOverflow" : false});
        }
        {
            var Q0;
            {var subQ0=sQuery(id+"F4.wireOp",EDGE,"E33.trimOffspring");var subQ1=sQuery(id+"F4.wireOp",EDGE,"E32.trimOffspring");var subQ2=sQuery(id+"F4.wireOp",EDGE,"E31.trimOffspring");var subQ3=sQuery(id+"F4.wireOp",EDGE,"E30.trimOffspring");var subQ4=sQuery(id+"F4.wireOp",EDGE,"E28");var subQ5=sQuery(id+"F4.wireOp",EDGE,"E27");var subQ6=sQuery(id+"F4.wireOp",EDGE,"E26");var subQ7=sQuery(id+"F4.wireOp",EDGE,"E25");var subQ8=sQuery(id+"F4.wireOp",EDGE,"E24");var subQ9=sQuery(id+"F4.wireOp",EDGE,"E23");var subQ10=sQuery(id+"F4.wireOp",EDGE,"E22");var subQ11=sQuery(id+"F4.wireOp",EDGE,"E21");var subQ12=sQuery(id+"F4.wireOp",EDGE,"E20.0");var subQ13=sQuery(id+"F4.wireOp",EDGE,"E19.0");var subQ14=sQuery(id+"F4.wireOp",EDGE,"E18.0");var subQ15=sQuery(id+"F4.wireOp",EDGE,"E17.0");var subQ16=sQuery(id+"F4.wireOp",EDGE,"E15");var subQ17=sQuery(id+"F4.wireOp",EDGE,"E14");var subQ18=sQuery(id+"F4.wireOp",EDGE,"E13");var subQ19=sQuery(id+"F4.wireOp",EDGE,"E12");Q0=makeQuery(id+"F19.opFillet","BLEND_EDGE",EDGE,{"blendedFrom":[makeQuery(id+"F7.opExtrude","SWEPT_EDGE",EDGE,{"disambiguationData":[OSD([subQ1,sQuery(id+"F5.wireOp",EDGE,"E44.MirrorCS"),sQuery(id+"F5.wireOp",EDGE,"E46.MirrorCS")])]}),makeQuery(id+"F7.boolean.opBoolean","MERGE",FACE,{"derivedFrom":[makeQuery(id+"F6.opExtrude","CAP_FACE",FACE,{"disambiguationData":[OSD([subQ19,subQ18,subQ17,subQ16,subQ15,subQ14,subQ13,subQ12,subQ11,subQ10,subQ9,subQ8,subQ7,subQ6,subQ5,subQ4,subQ3,subQ2,subQ1,subQ0])],"isStart":false}),makeQuery(id+"F7.opExtrude","CAP_FACE",FACE,{"disambiguationData":[OSD([subQ19,subQ18,subQ17,subQ16,subQ15,subQ14,subQ13,subQ12,subQ11,subQ10,subQ9,subQ8,subQ7,subQ6,subQ5,subQ4,subQ3,subQ2,subQ1,subQ0]),OD(0.0)],"isStart":false}),makeQuery(id+"F7.opExtrude","CAP_FACE",FACE,{"disambiguationData":[OSD([subQ19,subQ18,subQ17,subQ16,subQ15,subQ14,subQ13,subQ12,subQ11,subQ10,subQ9,subQ8,subQ7,subQ6,subQ5,subQ4,subQ3,subQ2,subQ1,subQ0]),OD(1.0)],"isStart":false}),makeQuery(id+"F7.opExtrude","CAP_FACE",FACE,{"disambiguationData":[OSD([subQ19,subQ18,subQ17,subQ16,subQ15,subQ14,subQ13,subQ12,subQ11,subQ10,subQ9,subQ8,subQ7,subQ6,subQ5,subQ4,subQ3,subQ2,subQ1,subQ0]),OD(2.0)],"isStart":false}),makeQuery(id+"F7.opExtrude","CAP_FACE",FACE,{"disambiguationData":[OSD([subQ19,subQ18,subQ17,subQ16,subQ15,subQ14,subQ13,subQ12,subQ11,subQ10,subQ9,subQ8,subQ7,subQ6,subQ5,subQ4,subQ3,subQ2,subQ1,subQ0]),OD(3.0)],"isStart":false})]})],"blendedInto":[makeQuery(id+"F7.boolean.opBoolean","MERGE",FACE,{"derivedFrom":[makeQuery(id+"F6.opExtrude","CAP_FACE",FACE,{"disambiguationData":[OSD([subQ19,subQ18,subQ17,subQ16,subQ15,subQ14,subQ13,subQ12,subQ11,subQ10,subQ9,subQ8,subQ7,subQ6,subQ5,subQ4,subQ3,subQ2,subQ1,subQ0])],"isStart":false}),makeQuery(id+"F7.opExtrude","CAP_FACE",FACE,{"disambiguationData":[OSD([subQ19,subQ18,subQ17,subQ16,subQ15,subQ14,subQ13,subQ12,subQ11,subQ10,subQ9,subQ8,subQ7,subQ6,subQ5,subQ4,subQ3,subQ2,subQ1,subQ0]),OD(0.0)],"isStart":false}),makeQuery(id+"F7.opExtrude","CAP_FACE",FACE,{"disambiguationData":[OSD([subQ19,subQ18,subQ17,subQ16,subQ15,subQ14,subQ13,subQ12,subQ11,subQ10,subQ9,subQ8,subQ7,subQ6,subQ5,subQ4,subQ3,subQ2,subQ1,subQ0]),OD(1.0)],"isStart":false}),makeQuery(id+"F7.opExtrude","CAP_FACE",FACE,{"disambiguationData":[OSD([subQ19,subQ18,subQ17,subQ16,subQ15,subQ14,subQ13,subQ12,subQ11,subQ10,subQ9,subQ8,subQ7,subQ6,subQ5,subQ4,subQ3,subQ2,subQ1,subQ0]),OD(2.0)],"isStart":false}),makeQuery(id+"F7.opExtrude","CAP_FACE",FACE,{"disambiguationData":[OSD([subQ19,subQ18,subQ17,subQ16,subQ15,subQ14,subQ13,subQ12,subQ11,subQ10,subQ9,subQ8,subQ7,subQ6,subQ5,subQ4,subQ3,subQ2,subQ1,subQ0]),OD(3.0)],"isStart":false})]})]});}
            var Q1;
            Q1=makeQuery(id+"F6.opExtrude","CAP_EDGE",EDGE,{"disambiguationData":[OSD([sQuery(id+"F4.wireOp",EDGE,"E23")])],"isStart":false});
            var Q2;
            Q2=makeQuery(id+"F6.opExtrude","CAP_EDGE",EDGE,{"disambiguationData":[OSD([sQuery(id+"F4.wireOp",EDGE,"E21")])],"isStart":false});
            var Q3;
            Q3=makeQuery(id+"F6.opExtrude","CAP_EDGE",EDGE,{"disambiguationData":[OSD([sQuery(id+"F4.wireOp",EDGE,"E28")])],"isStart":false});
            var Q4;
            Q4=makeQuery(id+"F6.opExtrude","CAP_EDGE",EDGE,{"disambiguationData":[OSD([sQuery(id+"F4.wireOp",EDGE,"E14")])],"isStart":false});
            var Q5;
            Q5=makeQuery(id+"F6.opExtrude","CAP_EDGE",EDGE,{"disambiguationData":[OSD([sQuery(id+"F4.wireOp",EDGE,"E29.0")])],"isStart":false});
            var Q6;
            Q6=makeQuery(id+"F6.opExtrude","CAP_EDGE",EDGE,{"disambiguationData":[OSD([sQuery(id+"F4.wireOp",EDGE,"E16")])],"isStart":false});
            chamfer(context, id + "F20", {"entities" : qUnion([Q0, Q1, Q2, Q3, Q4, Q5, Q6]), "width" : 1 * mm, "tangentPropagation" : true});
        }
    });
